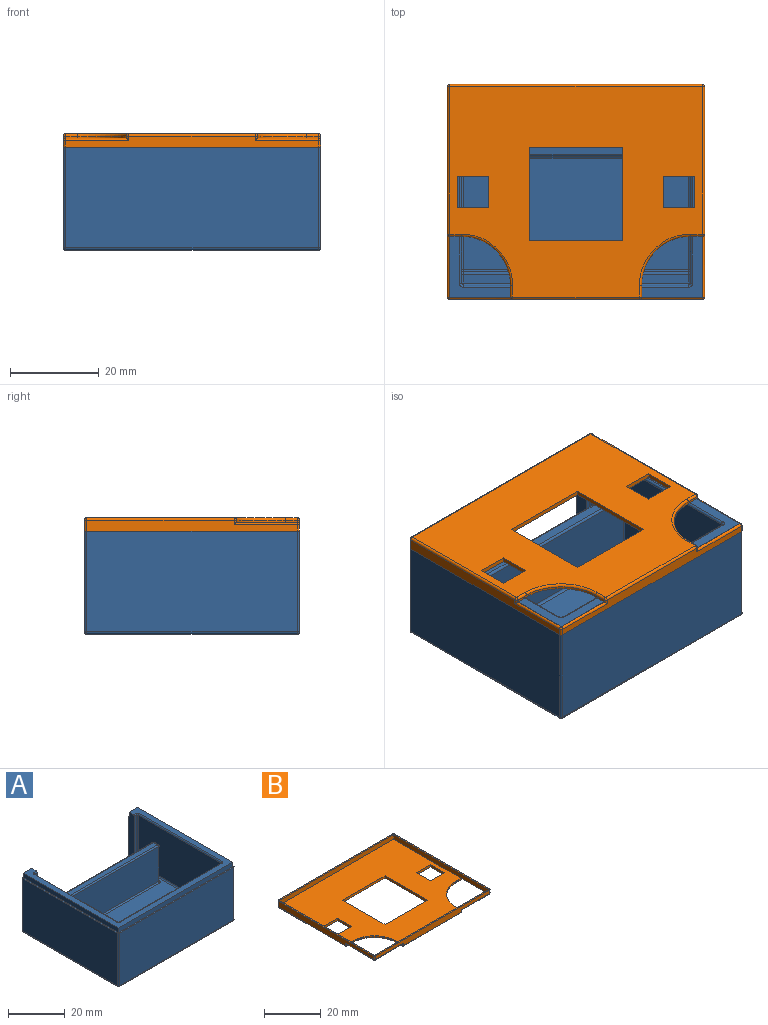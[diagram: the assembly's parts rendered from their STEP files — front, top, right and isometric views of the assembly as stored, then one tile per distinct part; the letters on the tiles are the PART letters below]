
ASSEMBLY  parts=2 mates=1
PART A: 90 faces, bbox 57.9x48.4x25.2 mm
  f0: plane 56.85x22.68mm, normal (0,1,0), area 319.1mm2, adj f4,f6,f8,f14,f78,f83,f84
  f1: plane 47.35x22.68mm, normal (1,0,0), area 1073.7mm2, adj f4,f5,f75,f84
  f2: plane 47.35x22.68mm, normal (-1,0,0), area 1073.7mm2, adj f6,f7,f82,f84
  f3: plane 56.85x22.68mm, normal (0,-1,0), area 1289.1mm2, adj f5,f7,f79,f84
  f4: cylinder r=0.5mm len=22.68mm, axis (0,0,1), area 17.8mm2, adj f0,f1,f76,f84
  f5: cylinder r=0.5mm len=22.68mm, axis (0,0,-1), area 17.8mm2, adj f1,f3,f77,f84
  f6: cylinder r=0.5mm len=22.68mm, axis (0,0,-1), area 17.8mm2, adj f0,f2,f80,f84
  f7: cylinder r=0.5mm len=22.68mm, axis (0,0,1), area 17.8mm2, adj f2,f3,f81,f84
  f8: plane 22x3.68mm, normal (-1,0,0), area 68.8mm2, adj f0,f9,f10,f11,f13,f14,f84,f85
  f9: plane 21x1mm, normal (0,-1,0), area 21mm2, adj f8,f11,f13,f46
  f10: plane 56.85x47.35mm, normal (0,0,1), area 329.7mm2, adj f8,f11,f12,f26,f27,f30,f32,f34
  f11: cylinder r=0.5mm len=1mm, axis (-1,0,0), area 0.8mm2, adj f8,f9,f10,f37
  f12: cylinder r=0.5mm len=1mm, axis (-1,0,0), area 0.8mm2, adj f10,f16,f27,f83
  f13: cylinder r=0.5mm len=1mm, axis (1,0,0), area 0.8mm2, adj f8,f9,f14,f53
  f14: plane 50.5x41.68mm, normal (0,0,1), area 1899.7mm2, adj f0,f8,f13,f28,f44,f45,f52,f59
  f15: plane 41x21mm, normal (-1,0,0), area 813.2mm2, adj f30,f31,f46,f47,f54,f60,f61
  f16: plane 21x1mm, normal (0,-1,0), area 21mm2, adj f12,f29,f45,f83
  f17: plane 50.5x5mm, normal (0,1,0), area 252.5mm2, adj f31,f32,f48,f49
  f18: plane 41x21mm, normal (1,0,0), area 749.6mm2, adj f28,f29,f34,f40,f49,f50,f56,f63
  f19: plane 56.85x47.35mm, normal (0,0,-1), area 2691.8mm2, adj f75,f78,f79,f82
  f20: plane 50.5x15mm, normal (0,1,0), area 757.5mm2, adj f61,f62,f70,f71
  f21: plane 50.5x2mm, normal (0,0,1), area 101mm2, adj f47,f48,f62,f63
  f22: plane 48.5x15mm, normal (0,-1,0), area 727.5mm2, adj f57,f58,f68,f69
  f23: plane 15x2mm, normal (1,0,0), area 30mm2, adj f42,f43,f58,f59
  f24: plane 48.5x15mm, normal (0,1,0), area 727.5mm2, adj f40,f41,f43,f44
  f25: plane 48.5x2mm, normal (0,0,1), area 97mm2, adj f41,f42,f56,f57
  f26: torus R=1mm, axis (0,0,1), area 0.8mm2, adj f10,f30,f31,f32
  f27: torus R=1mm, axis (0,0,1), area 0.8mm2, adj f10,f12,f29,f34
  f28: cylinder r=0.5mm len=9mm, axis (0,1,0), area 7.1mm2, adj f14,f18,f35,f36
  f29: cylinder r=0.5mm len=21mm, axis (0,0,1), area 16.5mm2, adj f16,f18,f27,f36
  f30: cylinder r=0.5mm len=41mm, axis (0,1,0), area 32.2mm2, adj f10,f15,f26,f37
  f31: cylinder r=0.5mm len=5mm, axis (0,0,1), area 3.9mm2, adj f15,f17,f26,f38
  f32: cylinder r=0.5mm len=50.5mm, axis (1,0,0), area 39.7mm2, adj f10,f17,f26,f39
  f33: sphere r=0.5mm, area 0.4mm2, adj f41,f42,f43
  f34: cylinder r=0.5mm len=41mm, axis (0,-1,0), area 32.2mm2, adj f10,f18,f27,f39
  f35: sphere r=0.5mm, area 0.4mm2, adj f28,f40,f44
  f36: sphere r=0.5mm, area 0.4mm2, adj f28,f29,f45
  f37: torus R=1mm, axis (0,0,1), area 0.8mm2, adj f10,f11,f30,f46
  f38: sphere r=0.5mm, area 0.4mm2, adj f31,f47,f48
  f39: torus R=1mm, axis (0,0,1), area 0.8mm2, adj f10,f32,f34,f49
  f40: cylinder r=0.5mm len=15mm, axis (0,0,-1), area 11.8mm2, adj f18,f24,f35,f50
  f41: cylinder r=0.5mm len=48.5mm, axis (1,0,0), area 38.1mm2, adj f24,f25,f33,f50
  f42: cylinder r=0.5mm len=2mm, axis (0,-1,0), area 1.6mm2, adj f23,f25,f33,f51
  f43: cylinder r=0.5mm len=15mm, axis (0,0,-1), area 11.8mm2, adj f23,f24,f33,f52
  f44: cylinder r=0.5mm len=48.5mm, axis (-1,0,0), area 38.1mm2, adj f14,f24,f35,f52
  f45: cylinder r=0.5mm len=1mm, axis (1,0,0), area 0.8mm2, adj f14,f16,f36,f83
  f46: cylinder r=0.5mm len=21mm, axis (0,0,-1), area 16.5mm2, adj f9,f15,f37,f53
  f47: cylinder r=0.5mm len=2mm, axis (0,-1,0), area 1.6mm2, adj f15,f21,f38,f54
  f48: cylinder r=0.5mm len=50.5mm, axis (-1,0,0), area 39.7mm2, adj f17,f21,f38,f55
  f49: cylinder r=0.5mm len=5mm, axis (0,0,-1), area 3.9mm2, adj f17,f18,f39,f55
  f50: torus R=1mm, axis (1,0,0), area 0.8mm2, adj f18,f40,f41,f56
  f51: sphere r=0.5mm, area 0.4mm2, adj f42,f57,f58
  f52: torus R=1mm, axis (0,0,1), area 0.8mm2, adj f14,f43,f44,f59
  f53: sphere r=0.5mm, area 0.4mm2, adj f13,f46,f60
  f54: torus R=1mm, axis (1,0,0), area 0.8mm2, adj f15,f47,f61,f62
  f55: sphere r=0.5mm, area 0.4mm2, adj f48,f49,f63
  f56: cylinder r=0.5mm len=2mm, axis (0,1,0), area 1.6mm2, adj f18,f25,f50,f64
  f57: cylinder r=0.5mm len=48.5mm, axis (-1,0,0), area 38.1mm2, adj f22,f25,f51,f64
  f58: cylinder r=0.5mm len=15mm, axis (0,0,1), area 11.8mm2, adj f22,f23,f51,f65
  f59: cylinder r=0.5mm len=2mm, axis (0,1,0), area 1.6mm2, adj f14,f23,f52,f65
  f60: cylinder r=0.5mm len=38mm, axis (0,-1,0), area 29.8mm2, adj f14,f15,f53,f66
  f61: cylinder r=0.5mm len=15mm, axis (0,0,1), area 11.8mm2, adj f15,f20,f54,f66
  f62: cylinder r=0.5mm len=50.5mm, axis (1,0,0), area 39.7mm2, adj f20,f21,f54,f67
  f63: cylinder r=0.5mm len=2mm, axis (0,1,0), area 1.6mm2, adj f18,f21,f55,f67
  f64: torus R=1mm, axis (1,0,0), area 0.8mm2, adj f18,f56,f57,f68
  f65: torus R=1mm, axis (0,0,1), area 0.8mm2, adj f14,f58,f59,f69
  f66: sphere r=0.5mm, area 0.4mm2, adj f60,f61,f70
  f67: torus R=1mm, axis (1,0,0), area 0.8mm2, adj f18,f62,f63,f71
  f68: cylinder r=0.5mm len=15mm, axis (0,0,1), area 11.8mm2, adj f18,f22,f64,f72
  f69: cylinder r=0.5mm len=48.5mm, axis (1,0,0), area 38.1mm2, adj f14,f22,f65,f72
  f70: cylinder r=0.5mm len=50.5mm, axis (-1,0,0), area 39.7mm2, adj f14,f20,f66,f73
  f71: cylinder r=0.5mm len=15mm, axis (0,0,-1), area 11.8mm2, adj f18,f20,f67,f73
  f72: sphere r=0.5mm, area 0.4mm2, adj f68,f69,f74
  f73: sphere r=0.5mm, area 0.4mm2, adj f70,f71,f74
  f74: cylinder r=0.5mm len=25mm, axis (0,1,0), area 19.6mm2, adj f14,f18,f72,f73
  f75: cylinder r=0.5mm len=47.35mm, axis (0,1,0), area 37.2mm2, adj f1,f19,f76,f77
  f76: sphere r=0.5mm, area 0.4mm2, adj f4,f75,f78
  f77: sphere r=0.5mm, area 0.4mm2, adj f5,f75,f79
  f78: cylinder r=0.5mm len=56.85mm, axis (-1,0,0), area 44.6mm2, adj f0,f19,f76,f80
  f79: cylinder r=0.5mm len=56.85mm, axis (1,0,0), area 44.6mm2, adj f3,f19,f77,f81
  f80: sphere r=0.5mm, area 0.4mm2, adj f6,f78,f82
  f81: sphere r=0.5mm, area 0.4mm2, adj f7,f79,f82
  f82: cylinder r=0.5mm len=47.35mm, axis (0,-1,0), area 37.2mm2, adj f2,f19,f80,f81
  f83: plane 22x3.68mm, normal (1,0,0), area 68.9mm2, adj f0,f10,f12,f14,f16,f45,f84,f89
  f84: plane 57.85x48.35mm, normal (0,0,1), area 80.7mm2, adj f0,f1,f2,f3,f4,f5,f6,f7
  f85: plane 4.18x2mm, normal (0,1,0), area 8.3mm2, adj f8,f10,f84,f86
  f86: plane 47.35x2mm, normal (1,0,0), area 94.7mm2, adj f10,f84,f85,f87
  f87: plane 56.85x2mm, normal (0,-1,0), area 113.7mm2, adj f10,f84,f86,f88
  f88: plane 47.35x2mm, normal (-1,0,0), area 94.7mm2, adj f10,f84,f87,f89
  f89: plane 4.18x2mm, normal (0,1,0), area 8.3mm2, adj f10,f83,f84,f88
PART B: 59 faces, bbox 57.9x48.4x3 mm
  f0: plane 56.85x2mm, normal (0,-1,0), area 113.7mm2, adj f1,f7,f8,f9
  f1: plane 47.35x2mm, normal (-1,0,0), area 94.7mm2, adj f0,f2,f8,f9,f44
  f2: plane 56.85x2mm, normal (0,1,0), area 113.7mm2, adj f1,f7,f8,f9,f42,f52
  f3: plane 56.85x2.5mm, normal (0,-1,0), area 113.8mm2, adj f8,f35,f42,f43,f48,f52,f54,f55
  f4: plane 47.35x2.5mm, normal (1,0,0), area 104.2mm2, adj f8,f36,f43,f44,f45,f46
  f5: plane 56.85x2.5mm, normal (0,1,0), area 142.1mm2, adj f8,f29,f36,f37
  f6: plane 47.35x2.5mm, normal (-1,0,0), area 104.2mm2, adj f8,f29,f30,f31,f34,f35
  f7: plane 47.35x2mm, normal (1,0,0), area 94.7mm2, adj f0,f2,f8,f9,f34
  f8: plane 57.85x48.35mm, normal (0,0,1), area 105mm2, adj f0,f1,f2,f3,f4,f5,f6,f7
  f9: plane 56.85x47.35mm, normal (0,0,1), area 1830.8mm2, adj f0,f1,f2,f7,f10,f11,f12,f13
  f10: plane 21x1mm, normal (1,0,0), area 21mm2, adj f9,f11,f27,f28
  f11: plane 21x1mm, normal (0,-1,0), area 21mm2, adj f9,f10,f12,f28
  f12: plane 21x1mm, normal (-1,0,0), area 21mm2, adj f9,f11,f27,f28
  f13: plane 7x1mm, normal (1,0,0), area 7mm2, adj f9,f14,f24,f28
  f14: plane 7x1mm, normal (0,-1,0), area 7mm2, adj f9,f13,f15,f28
  f15: plane 7x1mm, normal (-1,0,0), area 7mm2, adj f9,f14,f24,f28
  f16: plane 7x1mm, normal (0,-1,0), area 7mm2, adj f9,f17,f25,f28
  f17: plane 7x1mm, normal (-1,0,0), area 7mm2, adj f9,f16,f18,f28
  f18: plane 7x1mm, normal (0,1,0), area 7mm2, adj f9,f17,f25,f28
  f19: cylinder r=11mm len=11mm, axis (0,0,1), area 8.6mm2, adj f9,f20,f26,f56
  f20: plane 2.68x0.5mm, normal (0,-1,0), area 1.3mm2, adj f9,f19,f45,f53
  f21: plane 2.68x0.5mm, normal (0,-1,0), area 1.3mm2, adj f9,f22,f31,f38
  f22: cylinder r=11mm len=11mm, axis (0,0,1), area 8.6mm2, adj f9,f21,f23,f41
  f23: plane 2.68x0.5mm, normal (-1,0,0), area 1.3mm2, adj f9,f22,f47,f48
  f24: plane 7x1mm, normal (0,1,0), area 7mm2, adj f9,f13,f15,f28
  f25: plane 7x1mm, normal (1,0,0), area 7mm2, adj f9,f16,f18,f28
  f26: plane 2.68x0.5mm, normal (1,0,0), area 1.3mm2, adj f9,f19,f55,f58
  f27: plane 21x1mm, normal (0,1,0), area 21mm2, adj f9,f10,f12,f28
  f28: plane 56.85x47.35mm, normal (0,0,-1), area 1807.7mm2, adj f10,f11,f12,f13,f14,f15,f16,f17
  f29: cylinder r=0.5mm len=2.5mm, axis (0,0,-1), area 2mm2, adj f5,f6,f8,f32
  f30: cylinder r=0.5mm len=33.18mm, axis (0,-1,0), area 26.1mm2, adj f6,f28,f32,f33
  f31: cylinder r=0.5mm len=1mm, axis (0,0,1), area 0.5mm2, adj f6,f21,f33,f34
  f32: sphere r=0.5mm, area 0.4mm2, adj f29,f30,f37
  f33: sphere r=0.5mm, area 0.4mm2, adj f30,f31,f38
  f34: cylinder r=0.5mm len=14.18mm, axis (0,-1,0), area 10.9mm2, adj f6,f7,f31,f39
  f35: cylinder r=0.5mm len=1.5mm, axis (0,0,1), area 1.2mm2, adj f3,f6,f8,f39
  f36: cylinder r=0.5mm len=2.5mm, axis (0,0,1), area 2mm2, adj f4,f5,f8,f40
  f37: cylinder r=0.5mm len=56.85mm, axis (-1,0,0), area 44.6mm2, adj f5,f28,f32,f40
  f38: cylinder r=0.5mm len=2.68mm, axis (-1,0,0), area 2.1mm2, adj f21,f28,f33,f41
  f39: sphere r=0.5mm, area 0.4mm2, adj f34,f35,f42
  f40: sphere r=0.5mm, area 0.4mm2, adj f36,f37,f46
  f41: torus R=11.5mm, axis (0,0,1), area 13.8mm2, adj f22,f28,f38,f47
  f42: cylinder r=0.5mm len=14.18mm, axis (1,0,0), area 10.9mm2, adj f2,f3,f39,f48
  f43: cylinder r=0.5mm len=1.5mm, axis (0,0,-1), area 1.2mm2, adj f3,f4,f8,f49
  f44: cylinder r=0.5mm len=14.18mm, axis (0,1,0), area 10.9mm2, adj f1,f4,f45,f49
  f45: cylinder r=0.5mm len=1mm, axis (0,0,1), area 0.5mm2, adj f4,f20,f44,f50
  f46: cylinder r=0.5mm len=33.18mm, axis (0,1,0), area 26.1mm2, adj f4,f28,f40,f50
  f47: cylinder r=0.5mm len=2.68mm, axis (0,1,0), area 2.1mm2, adj f23,f28,f41,f51
  f48: cylinder r=0.5mm len=1mm, axis (0,0,1), area 0.5mm2, adj f3,f23,f42,f51
  f49: sphere r=0.5mm, area 0.4mm2, adj f43,f44,f52
  f50: sphere r=0.5mm, area 0.4mm2, adj f45,f46,f53
  f51: sphere r=0.5mm, area 0.4mm2, adj f47,f48,f54
  f52: cylinder r=0.5mm len=14.18mm, axis (1,0,0), area 10.9mm2, adj f2,f3,f49,f55
  f53: cylinder r=0.5mm len=2.68mm, axis (-1,0,0), area 2.1mm2, adj f20,f28,f50,f56
  f54: cylinder r=0.5mm len=28.5mm, axis (1,0,0), area 22.4mm2, adj f3,f28,f51,f57
  f55: cylinder r=0.5mm len=1mm, axis (0,0,-1), area 0.5mm2, adj f3,f26,f52,f57
  f56: torus R=11.5mm, axis (0,0,1), area 13.8mm2, adj f19,f28,f53,f58
  f57: sphere r=0.5mm, area 0.4mm2, adj f54,f55,f58
  f58: cylinder r=0.5mm len=2.68mm, axis (0,-1,0), area 2.1mm2, adj f26,f28,f56,f57
PLACE A t=(-6.94,10.91,21.46)mm fixed
PLACE B rot(axis=(0,1,0),180deg) t=(-6.94,10.91,43.46)mm
MATE slider B.f9 <-> A.f10  axis (0,0,-1) through (-6.94,-12.76,43.46)mm
